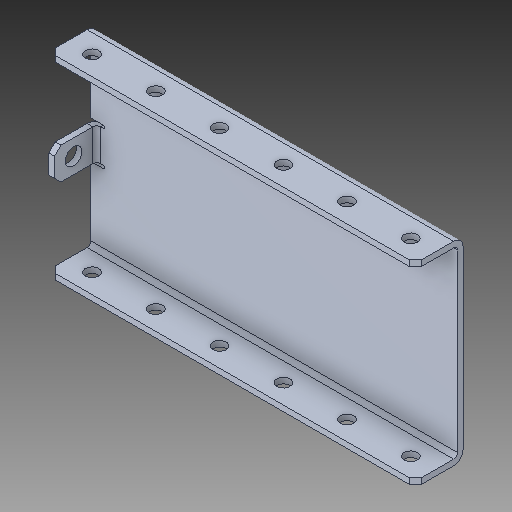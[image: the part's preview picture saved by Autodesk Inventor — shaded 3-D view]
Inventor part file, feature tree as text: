
AUTODESK INVENTOR PART (.ipt)
format: ipt  version: 2018 (Build 220112000, 112)  size: 157,696 bytes
history: native  units: in
note: dims shown in document units (in); Inventor stores cm internally (conversion verified against a paired STEP export)
features: chamfer x1
ambient origin geometry x8: Origin, YZ Plane, XZ Plane, XY Plane, X Axis, Y Axis, Z Axis, Center Point
bodies: Solid1 (feature_tree)
feature tree (1):
  chamfer  "Chamfer1"  [1 undecoded]
note: 1 required parameter value undecoded (feature->parameter linkage not recoverable at this tier; creation-order binding heuristic only, values carry confidence <= 0.55)
